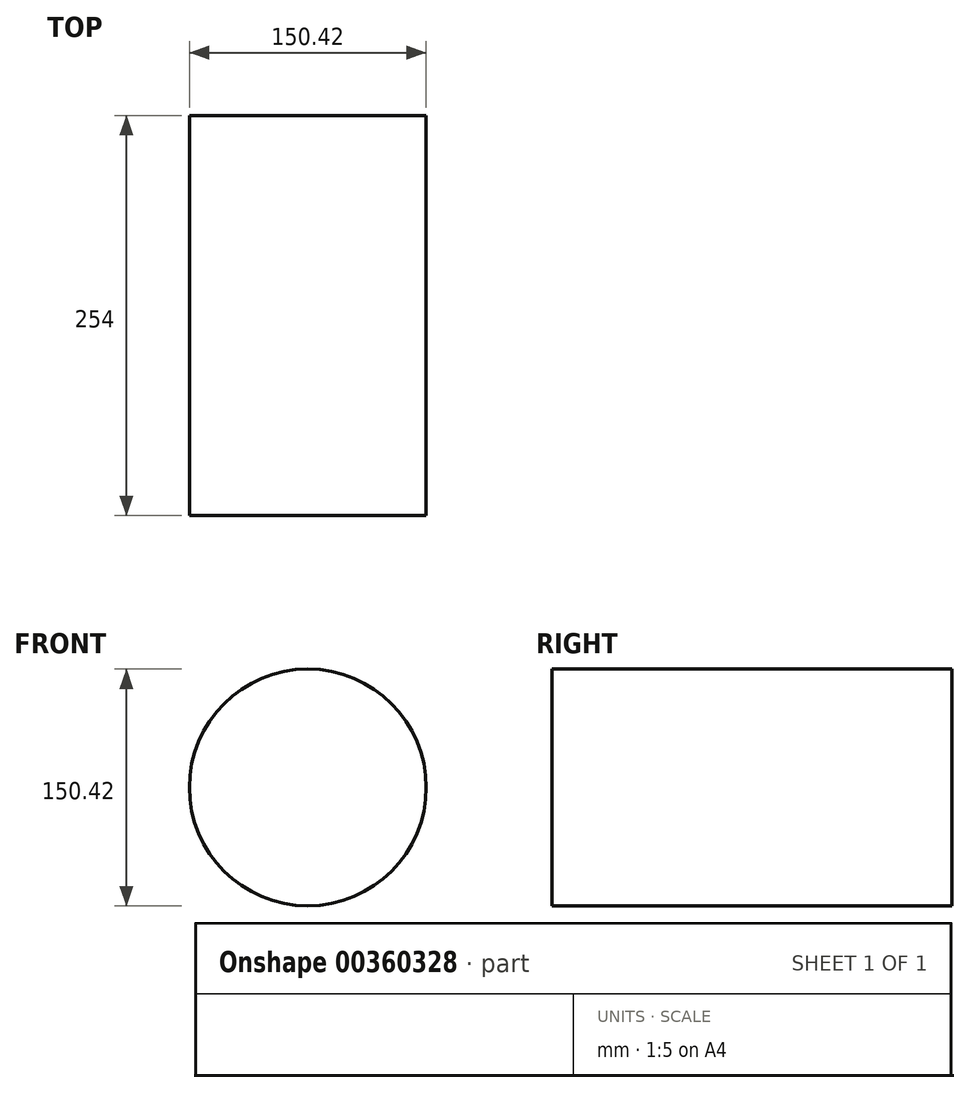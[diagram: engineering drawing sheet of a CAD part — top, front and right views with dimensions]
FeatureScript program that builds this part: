
annotation { "Feature Type Name" : "Feature", "Feature Type Description" : "" }
export const myFeature = defineFeature(function(context is Context, id is Id, definition is map)
    precondition{}
    {
        {
            var Q0;
            Q0=qCreatedBy(makeId("Front.planeOp"),FACE);
            var sketch = newSketch(context, id + "F0", { "sketchPlane" : qUnion([Q0])});
            skCircle(sketch, "E0", {"center": v(0, 0) * mm, "radius": 75.2 * mm});
            skSolve(sketch);
        }
        {
            var Q0;
            Q0=makeQuery(id+"F0.imprint","IMPRINT",FACE,{"disambiguationData":[TD([[makeQuery(id+"F0.imprint","IMPRINT",EDGE,{"derivedFrom":sQuery(id+"F0.wireOp",EDGE,"E0")}),1.0]])]});
            var sketch = newSketch(context, id + "F1", { "sketchPlane" : qUnion([Q0])});
            skSolve(sketch);
        }
        {
            var Q0;
            Q0=makeQuery(id+"F1.imprint","IMPRINT",FACE,{"disambiguationData":[TD([[makeQuery(id+"F1.imprint","IMPRINT",EDGE,{"derivedFrom":makeQuery(id+"F0.imprint","IMPRINT",EDGE,{"derivedFrom":sQuery(id+"F0.wireOp",EDGE,"E0")})}),1.0]])]});
            extrude(context, id + "F2", {"entities" : qUnion([Q0]), "depth" : 254 * mm});
        }
        {
            var Q0;
            Q0=makeQuery(id+"F2.opExtrude","CAP_FACE",FACE,{"disambiguationData":[OSD([sQuery(id+"F0.wireOp",EDGE,"E0")])],"isStart":false});
            var sketch = newSketch(context, id + "F3", { "sketchPlane" : qUnion([Q0])});
            skSolve(sketch);
        }
        {
            var Q0;
            Q0=makeQuery(id+"F3.imprint","IMPRINT",FACE,{"disambiguationData":[TD([[makeQuery(id+"F3.imprint","IMPRINT",EDGE,{"derivedFrom":makeQuery(id+"F2.opExtrude","CAP_EDGE",EDGE,{"disambiguationData":[OSD([sQuery(id+"F0.wireOp",EDGE,"E0")])],"isStart":false})}),1.0]])]});
            var sketch = newSketch(context, id + "F4", { "sketchPlane" : qUnion([Q0])});
            skCircle(sketch, "E1", {"center": v(0, 0) * mm, "radius": 1.22 * mm});
            skCircle(sketch, "E2", {"center": v(0, 0) * mm, "radius": 5.65 * mm});
            skCircle(sketch, "E3", {"center": v(0, 0) * mm, "radius": 67.33 * mm});
            skSolve(sketch);
        }
        {
            var Q0;
            Q0=sQuery(id+"F4.wireOp",EDGE,"E3");
            extrude(context, id + "F5", {"bodyType" : ToolBodyType.SURFACE, "surfaceEntities" : qUnion([Q0]), "endBound" : BoundingType.THROUGH_ALL, "oppositeDirection" : true, "depth" : 25.4 * mm});
        }
    });
